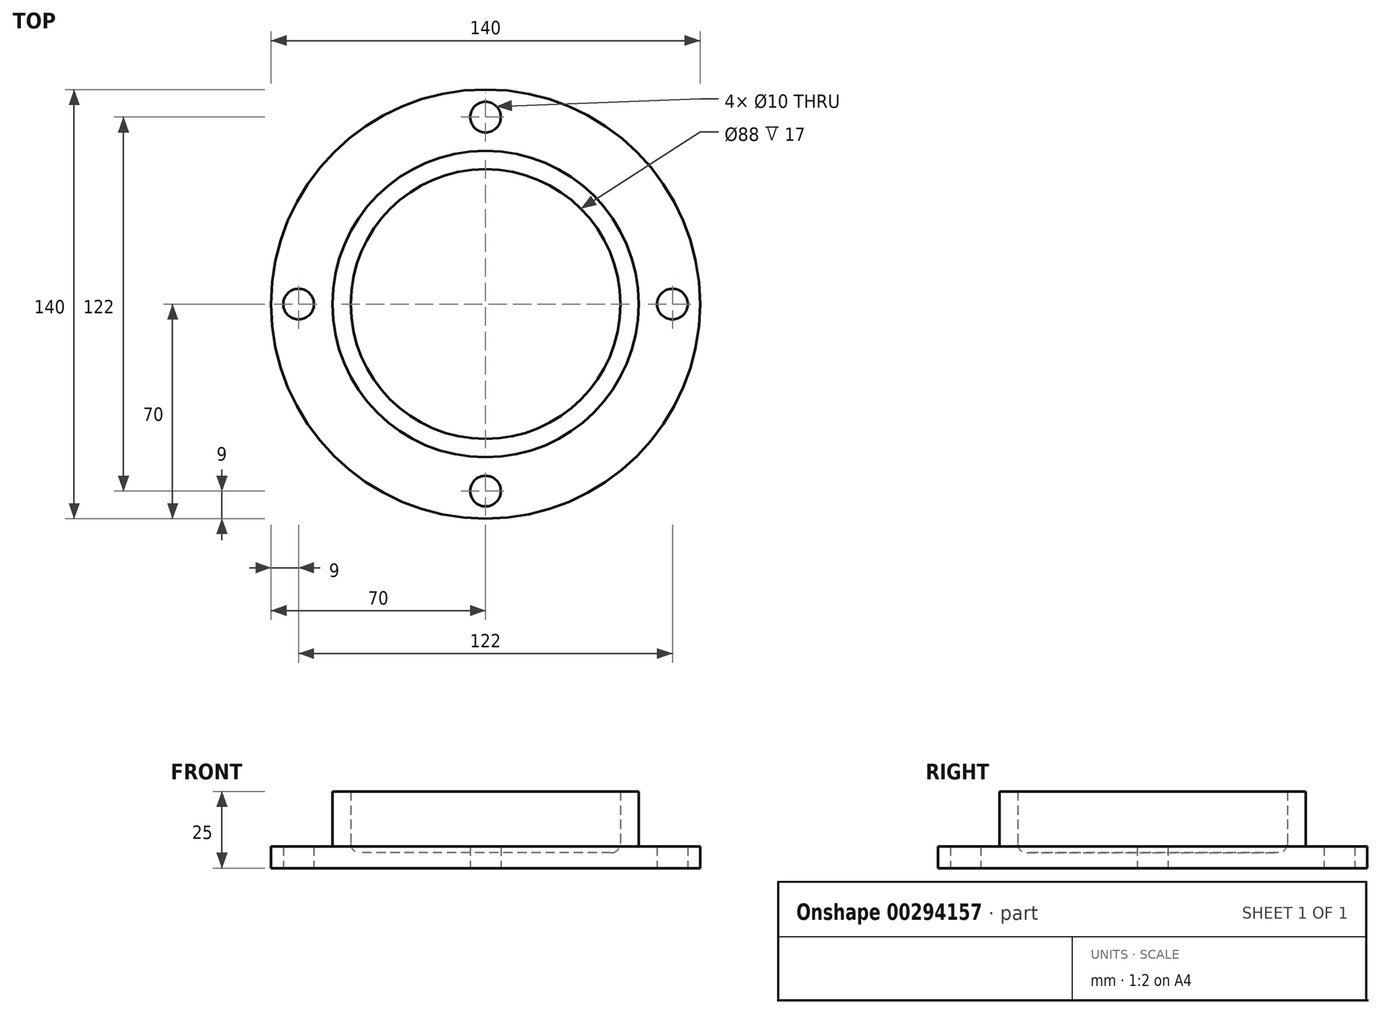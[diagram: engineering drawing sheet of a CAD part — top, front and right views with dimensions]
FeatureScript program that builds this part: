
annotation { "Feature Type Name" : "Feature", "Feature Type Description" : "" }
export const myFeature = defineFeature(function(context is Context, id is Id, definition is map)
    precondition{}
    {
        {
            var Q0;
            Q0=qCreatedBy(makeId("Top.planeOp"),FACE);
            var sketch = newSketch(context, id + "F0", { "sketchPlane" : qUnion([Q0])});
            skCircle(sketch, "E0", {"center": v(0, 0) * mm, "radius": 70 * mm});
            skPoint(sketch, "E1", {"position": v(0, 61) * mm});
            skPoint(sketch, "E2", {"position": v(0, -61) * mm});
            skPoint(sketch, "E3", {"position": v(61, 0) * mm});
            skPoint(sketch, "E4", {"position": v(-61, 0) * mm});
            skCircle(sketch, "E5", {"center": v(0, 61) * mm, "radius": 5 * mm});
            skCircle(sketch, "E6", {"center": v(-61, 0) * mm, "radius": 5 * mm});
            skCircle(sketch, "E7", {"center": v(0, -61) * mm, "radius": 5 * mm});
            skCircle(sketch, "E8", {"center": v(61, 0) * mm, "radius": 5 * mm});
            skSolve(sketch);
        }
        {
            var Q0;
            Q0 = qSketchRegion(id + "F0", true);
            extrude(context, id + "F1", {"entities" : qUnion([Q0]), "depth" : 7 * mm});
        }
        {
            var Q0;
            Q0=makeQuery(id+"F1.opExtrude","CAP_FACE",FACE,{"disambiguationData":[OSD([sQuery(id+"F0.wireOp",EDGE,"E0"),sQuery(id+"F0.wireOp",EDGE,"E5"),sQuery(id+"F0.wireOp",EDGE,"E6"),sQuery(id+"F0.wireOp",EDGE,"E7"),sQuery(id+"F0.wireOp",EDGE,"E8")])],"isStart":false});
            var sketch = newSketch(context, id + "F2", { "sketchPlane" : qUnion([Q0])});
            skCircle(sketch, "E9", {"center": v(0, 0) * mm, "radius": 50 * mm});
            skCircle(sketch, "E10", {"center": v(0, 0) * mm, "radius": 44 * mm});
            skSolve(sketch);
        }
        {
            var Q0;
            Q0 = qSketchRegion(id + "F2", true);
            extrude(context, id + "F3", {"entities" : qUnion([Q0]), "operationType" : NewBodyOperationType.ADD, "depth" : 18 * mm});
        }
        {
            var Q0;
            Q0=makeQuery(id+"F3.boolean.opBoolean","SPLIT",FACE,{"disambiguationData":[TD([makeQuery(id+"F3.opExtrude","SWEPT_FACE",FACE,{"disambiguationData":[OSD([sQuery(id+"F2.wireOp",EDGE,"E10")])]})])],"derivedFrom":makeQuery(id+"F1.opExtrude","CAP_FACE",FACE,{"disambiguationData":[OSD([sQuery(id+"F0.wireOp",EDGE,"E0"),sQuery(id+"F0.wireOp",EDGE,"E5"),sQuery(id+"F0.wireOp",EDGE,"E6"),sQuery(id+"F0.wireOp",EDGE,"E7"),sQuery(id+"F0.wireOp",EDGE,"E8")])],"isStart":false})});
            var sketch = newSketch(context, id + "F4", { "sketchPlane" : qUnion([Q0])});
            skCircle(sketch, "E11", {"center": v(0, 0) * mm, "radius": 44 * mm});
            skSolve(sketch);
        }
        {
            var Q0;
            Q0=makeQuery(id+"F4.imprint","IMPRINT",FACE,{"disambiguationData":[TD([[makeQuery(id+"F4.imprint","IMPRINT",EDGE,{"derivedFrom":sQuery(id+"F4.wireOp",EDGE,"E11")}),1.0]])]});
            extrude(context, id + "F5", {"entities" : qUnion([Q0]), "operationType" : NewBodyOperationType.REMOVE, "oppositeDirection" : true, "depth" : 2 * mm});
        }
        {
            var Q0;
            Q0=makeQuery(id+"F5.boolean.opBoolean","COPY",EDGE,{"derivedFrom":makeQuery(id+"F5.opExtrude","CAP_EDGE",EDGE,{"disambiguationData":[OSD([sQuery(id+"F4.wireOp",EDGE,"E11")])],"isStart":false})});
            fillet(context, id + "F6", {"entities" : qUnion([Q0]), "radius" : 3 * mm, "tangentPropagation" : true, "allowEdgeOverflow" : false});
        }
    });
